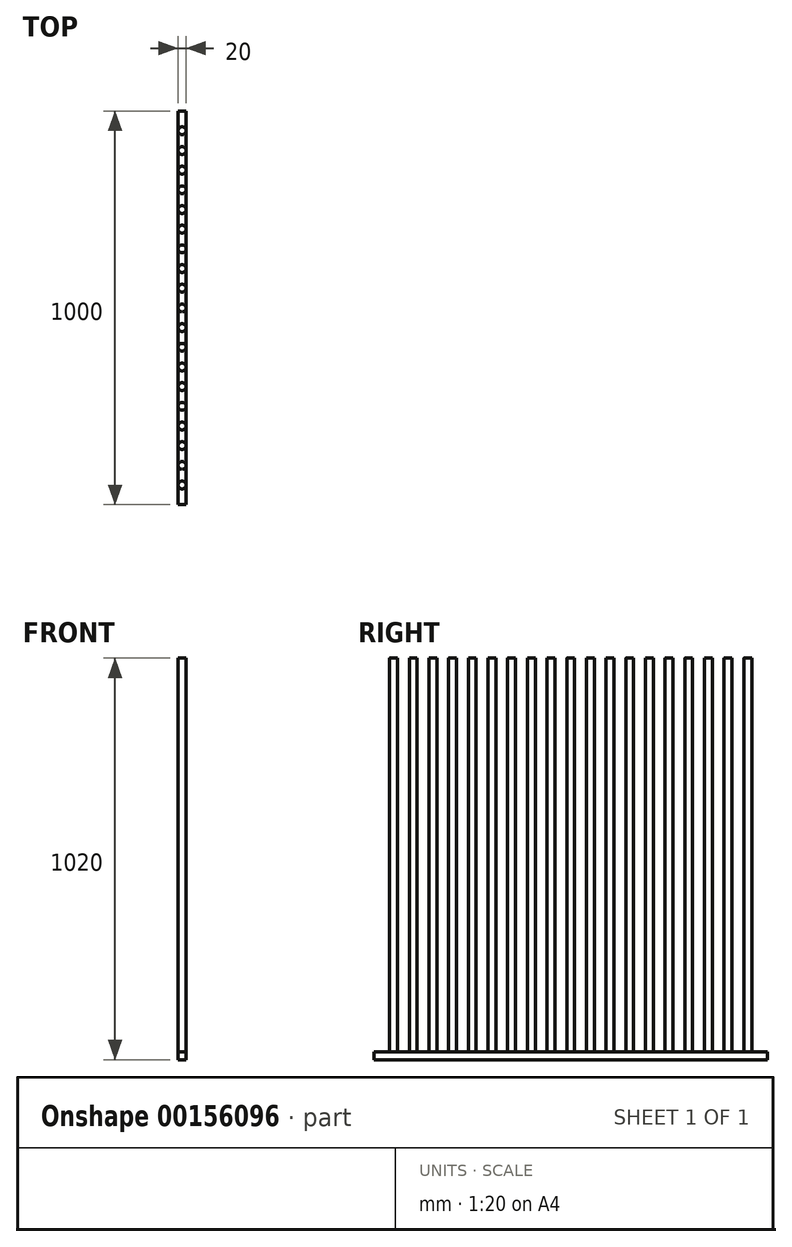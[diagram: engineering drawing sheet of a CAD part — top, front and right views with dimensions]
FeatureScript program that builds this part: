
annotation { "Feature Type Name" : "Feature", "Feature Type Description" : "" }
export const myFeature = defineFeature(function(context is Context, id is Id, definition is map)
    precondition{}
    {
        {
            var Q0;
            Q0=qCreatedBy(makeId("Front.planeOp"),FACE);
            var sketch = newSketch(context, id + "F0", { "sketchPlane" : qUnion([Q0])});
            skLineSegment(sketch, "E0.bottom", {"start": v(0, 0) * mm, "end": v(20, 0) * mm});
            skLineSegment(sketch, "E0.top", {"start": v(0, 20) * mm, "end": v(20, 20) * mm});
            skLineSegment(sketch, "E0.left", {"start": v(0, 0) * mm, "end": v(0, 20) * mm});
            skLineSegment(sketch, "E0.right", {"start": v(20, 0) * mm, "end": v(20, 20) * mm});
            skSolve(sketch);
        }
        {
            var Q0;
            Q0=makeQuery(id+"F0.imprint","IMPRINT",FACE,{"disambiguationData":[TD([[makeQuery(id+"F0.imprint","IMPRINT",EDGE,{"derivedFrom":sQuery(id+"F0.wireOp",EDGE,"E0.bottom")}),1.0]])]});
            extrude(context, id + "F1", {"entities" : qUnion([Q0]), "depth" : 1000 * mm});
        }
        {
            var Q0;
            Q0=makeQuery(id+"F1.opExtrude","SWEPT_FACE",FACE,{"disambiguationData":[OSD([sQuery(id+"F0.wireOp",EDGE,"E0.top")])]});
            var sketch = newSketch(context, id + "F2", { "sketchPlane" : qUnion([Q0])});
            skCircle(sketch, "E1", {"center": v(10, -50) * mm, "radius": 10 * mm});
            skCircle(sketch, "E2.0.1.0", {"center": v(10, -100) * mm, "radius": 10 * mm});
            skCircle(sketch, "E2.0.2.0", {"center": v(10, -150) * mm, "radius": 10 * mm});
            skCircle(sketch, "E2.0.3.0", {"center": v(10, -200) * mm, "radius": 10 * mm});
            skCircle(sketch, "E2.0.4.0", {"center": v(10, -250) * mm, "radius": 10 * mm});
            skCircle(sketch, "E2.0.5.0", {"center": v(10, -300) * mm, "radius": 10 * mm});
            skCircle(sketch, "E2.0.6.0", {"center": v(10, -350) * mm, "radius": 10 * mm});
            skCircle(sketch, "E2.0.7.0", {"center": v(10, -400) * mm, "radius": 10 * mm});
            skCircle(sketch, "E2.0.8.0", {"center": v(10, -450) * mm, "radius": 10 * mm});
            skCircle(sketch, "E2.0.9.0", {"center": v(10, -500) * mm, "radius": 10 * mm});
            skCircle(sketch, "E2.0.10.0", {"center": v(10, -550) * mm, "radius": 10 * mm});
            skCircle(sketch, "E2.0.11.0", {"center": v(10, -600) * mm, "radius": 10 * mm});
            skCircle(sketch, "E2.0.12.0", {"center": v(10, -650) * mm, "radius": 10 * mm});
            skCircle(sketch, "E2.0.13.0", {"center": v(10, -700) * mm, "radius": 10 * mm});
            skCircle(sketch, "E2.0.14.0", {"center": v(10, -750) * mm, "radius": 10 * mm});
            skCircle(sketch, "E2.0.15.0", {"center": v(10, -800) * mm, "radius": 10 * mm});
            skCircle(sketch, "E2.0.16.0", {"center": v(10, -850) * mm, "radius": 10 * mm});
            skCircle(sketch, "E2.0.17.0", {"center": v(10, -900) * mm, "radius": 10 * mm});
            skCircle(sketch, "E2.0.18.0", {"center": v(10, -950) * mm, "radius": 10 * mm});
            skLineSegment(sketch, "E2.direction1", {"start": v(10, -50) * mm, "end": v(-20.45, -50) * mm, "construction": true});
            skLineSegment(sketch, "E2.direction2", {"start": v(10, -50) * mm, "end": v(10, -100) * mm, "construction": true});
            skSolve(sketch);
        }
        {
            var Q0;
            Q0 = qSketchRegion(id + "F2", true);
            extrude(context, id + "F3", {"entities" : qUnion([Q0]), "operationType" : NewBodyOperationType.ADD, "depth" : 1000 * mm});
        }
    });
